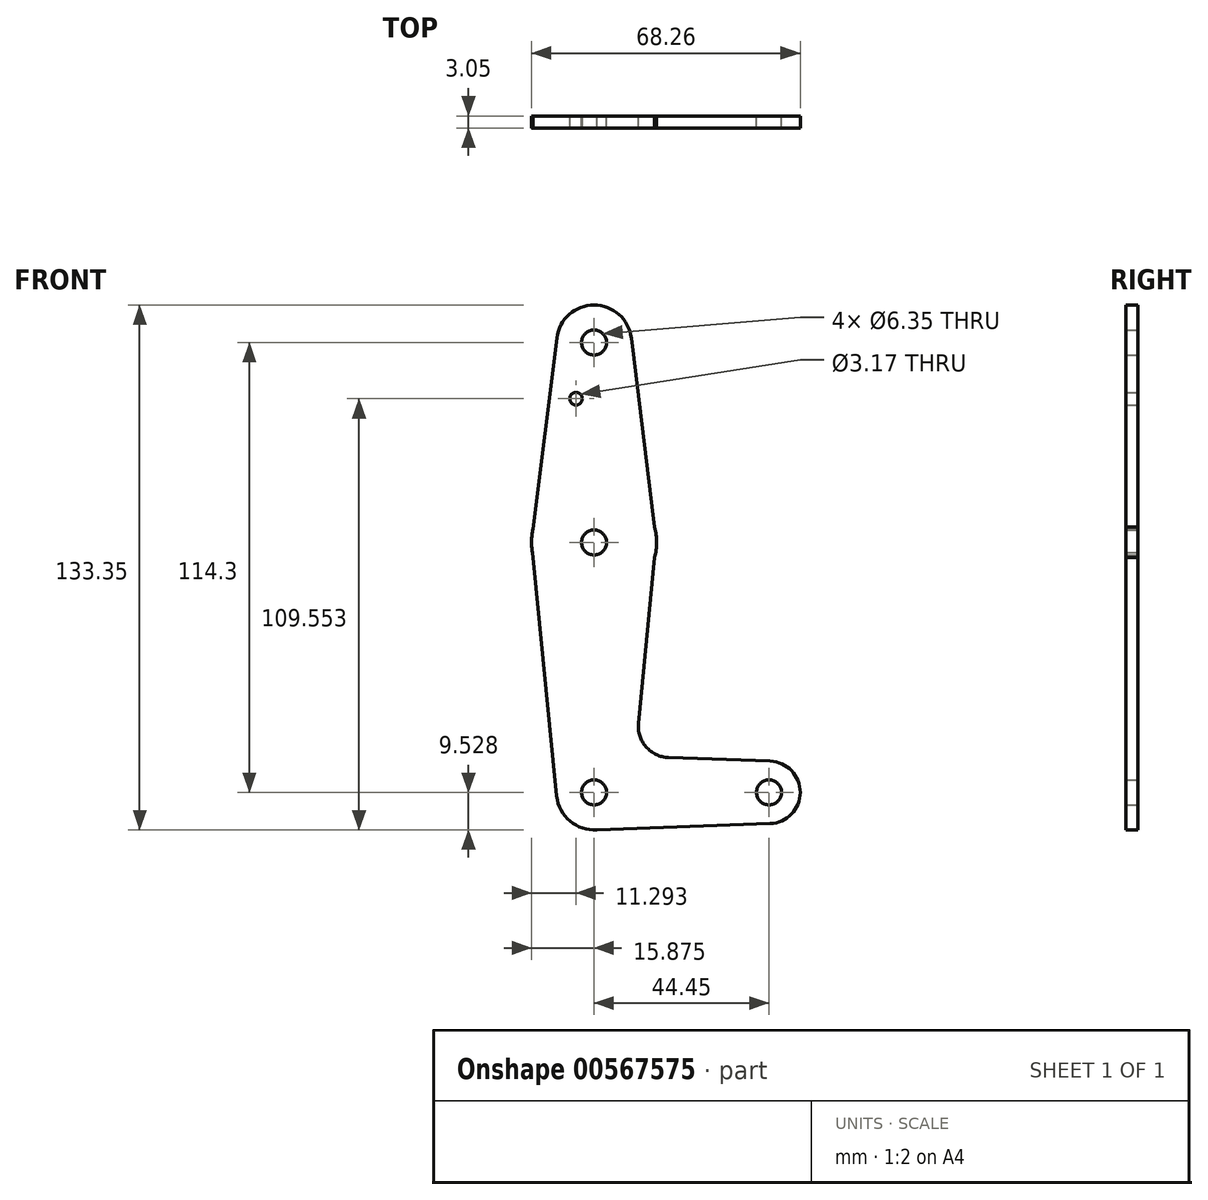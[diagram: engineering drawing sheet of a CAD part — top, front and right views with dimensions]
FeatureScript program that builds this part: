
annotation { "Feature Type Name" : "Feature", "Feature Type Description" : "" }
export const myFeature = defineFeature(function(context is Context, id is Id, definition is map)
    precondition{}
    {
        {
            var Q0;
            Q0=qCreatedBy(makeId("Front.planeOp"),FACE);
            var sketch = newSketch(context, id + "F0", { "sketchPlane" : qUnion([Q0])});
            skCircle(sketch, "E0", {"center": v(-36.9, -10) * mm, "radius": 9.53 * mm});
            skCircle(sketch, "E1", {"center": v(-36.9, 53.5) * mm, "radius": 15.88 * mm});
            skCircle(sketch, "E2", {"center": v(-36.9, 104.3) * mm, "radius": 9.53 * mm});
            skCircle(sketch, "E3", {"center": v(7.55, -10) * mm, "radius": 7.94 * mm});
            skLineSegment(sketch, "E4", {"start": v(-36.9, -10) * mm, "end": v(-36.9, 104.3) * mm, "construction": true});
            skLineSegment(sketch, "E5", {"start": v(-36.9, -10) * mm, "end": v(7.55, -10) * mm, "construction": true});
            skLineSegment(sketch, "E6", {"start": v(-52.76, 54) * mm, "end": v(-46.35, 105.48) * mm});
            skLineSegment(sketch, "E7", {"start": v(-21.02, 53.5) * mm, "end": v(-27.44, 105.47) * mm});
            skLineSegment(sketch, "E8", {"start": v(-52.56, 50.9) * mm, "end": v(-46.37, -10.95) * mm});
            skPoint(sketch, "E9.startSnap0", {"position": v(-36.9, 47.15) * mm});
            skLineSegment(sketch, "E10", {"start": v(-17.98, -1.15) * mm, "end": v(7.84, -2.07) * mm});
            skLineSegment(sketch, "E11", {"start": v(-36.96, -19.53) * mm, "end": v(7.84, -17.93) * mm});
            skLineSegment(sketch, "E12", {"start": v(-21.5, 49.66) * mm, "end": v(-25.6, 7.57) * mm});
            skCircle(sketch, "E13", {"center": v(-36.9, 104.3) * mm, "radius": 3.18 * mm});
            skCircle(sketch, "E14", {"center": v(-41.48, 90.02) * mm, "radius": 1.59 * mm});
            skCircle(sketch, "E15", {"center": v(-36.9, 53.5) * mm, "radius": 3.18 * mm});
            skCircle(sketch, "E16", {"center": v(-36.9, -10) * mm, "radius": 3.18 * mm});
            skCircle(sketch, "E17", {"center": v(7.55, -10) * mm, "radius": 3.18 * mm});
            skArc(sketch, "E18.filletArc", {"start": v(-25.6, 7.57) * mm, "mid": v(-23.68, 1.56) * mm, "end": v(-17.98, -1.15) * mm});
            skSolve(sketch);
        }
        {
            var Q0;
            Q0 = qSketchRegion(id + "F0", true);
            extrude(context, id + "F1", {"entities" : qUnion([Q0]), "depth" : 3.05 * mm, "offsetDistance" : 25.4 * mm});
        }
    });
